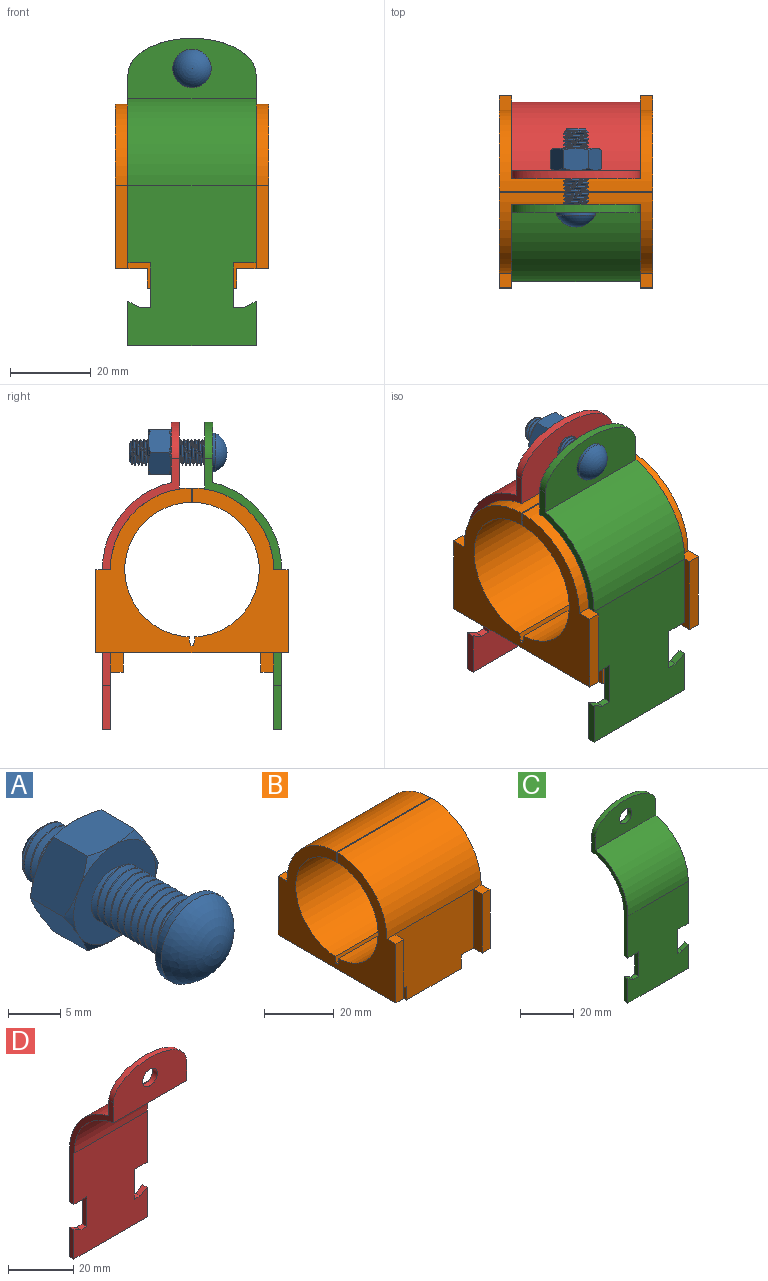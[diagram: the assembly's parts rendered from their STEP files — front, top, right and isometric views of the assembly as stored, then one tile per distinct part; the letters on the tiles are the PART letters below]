
ASSEMBLY  parts=4 mates=3
PART A: 34 faces, bbox 13.4x25x13.4 mm
  f0: cylinder r=3.17mm len=10.32mm, axis (0,-1,0), area 25.9mm2, adj f1,f3,f4,f8
  f1: bspline ~11.11x6.35mm, area 140.6mm2, adj f0,f2,f4,f8
  f2: cylinder r=2.59mm len=10.32mm, axis (0,-1,0), area 21.1mm2, adj f1,f3,f4,f8
  f3: bspline ~11.11x6.35mm, area 140.6mm2, adj f0,f2,f4,f8
  f4: plane 9.89x9.89mm, normal (0,1,0), area 45.1mm2, adj f0,f1,f2,f3,f5
  f5: cylinder r=4.76mm len=9.53mm, axis (0,1,0), area 22.8mm2, adj f4,f6
  f6: sphere r=5.32mm, area 98.5mm2, adj f5
  f7: plane 11.47x11.47mm, normal (0,1,0), area 70.8mm2, adj f15,f16,f17,f18,f19,f20,f30,f31
  f8: plane 11.47x11.47mm, normal (0,-1,0), area 70.8mm2, adj f0,f1,f2,f3,f21,f22,f23,f24
  f9: plane 6.09x6.08mm, normal (-0.87,0,0.5), area 33.4mm2, adj f10,f14,f15,f16,f21,f22
  f10: plane 6.95x6.08mm, normal (0,0,1), area 33.4mm2, adj f9,f11,f15,f20,f21,f26
  f11: plane 6.09x6.08mm, normal (0.87,0,0.5), area 33.4mm2, adj f10,f12,f19,f20,f25,f26
  f12: plane 6.09x6.08mm, normal (0.87,0,-0.5), area 33.4mm2, adj f11,f13,f18,f19,f24,f25
  f13: plane 6.95x6.08mm, normal (0,0,-1), area 33.4mm2, adj f12,f14,f17,f18,f23,f24
  f14: plane 6.09x6.08mm, normal (-0.87,0,-0.5), area 33.4mm2, adj f9,f13,f16,f17,f22,f23
  f15: cone r=5.56mm half-angle=60deg, axis (0,-1,0), area 3mm2, adj f7,f9,f10
  f16: cone r=5.56mm half-angle=60deg, axis (0,-1,0), area 3mm2, adj f7,f9,f14
  f17: cone r=5.56mm half-angle=60deg, axis (0,-1,0), area 3mm2, adj f7,f13,f14
  f18: cone r=5.56mm half-angle=60deg, axis (0,-1,0), area 3mm2, adj f7,f12,f13
  f19: cone r=5.56mm half-angle=60deg, axis (0,-1,0), area 3mm2, adj f7,f11,f12
  f20: cone r=5.56mm half-angle=60deg, axis (0,-1,0), area 3mm2, adj f7,f10,f11
  f21: cone r=5.56mm half-angle=60deg, axis (0,1,0), area 3mm2, adj f8,f9,f10
  f22: cone r=5.56mm half-angle=60deg, axis (0,1,0), area 3mm2, adj f8,f9,f14
  f23: cone r=5.56mm half-angle=60deg, axis (0,1,0), area 3mm2, adj f8,f13,f14
  f24: cone r=5.56mm half-angle=60deg, axis (0,1,0), area 3mm2, adj f8,f12,f13
  f25: cone r=5.56mm half-angle=60deg, axis (0,1,0), area 3mm2, adj f8,f11,f12
  f26: cone r=5.56mm half-angle=60deg, axis (0,1,0), area 3mm2, adj f8,f10,f11
  f27: plane 4.54x4.54mm, normal (0,1,0), area 16.2mm2, adj f28
  f28: cone r=3.17mm half-angle=45deg, axis (0,-1,0), area 12.5mm2, adj f27,f29,f30,f31,f32
  f29: cone r=3.17mm half-angle=45deg, axis (0,-1,0), area 1.7mm2, adj f28,f30,f32,f33
  f30: bspline ~6.35x6.35mm, area 56.5mm2, adj f7,f28,f29,f31,f33
  f31: cylinder r=2.59mm len=5.17mm, axis (0,-1,0), area 9.1mm2, adj f7,f28,f30,f32
  f32: bspline ~6.35x6.35mm, area 56.2mm2, adj f7,f28,f29,f31,f33
  f33: cylinder r=3.17mm len=6.35mm, axis (0,-1,0), area 9.6mm2, adj f7,f29,f30,f32
PART B: 35 faces, bbox 38.1x47.6x45.6 mm
  f0: plane 20.64x3.18mm, normal (0,-1,0), area 65.5mm2, adj f1,f11,f25,f30
  f1: plane 3.57x3.18mm, normal (0,0,1), area 11.3mm2, adj f0,f23,f25,f30
  f2: plane 20.64x3.18mm, normal (0,1,0), area 65.5mm2, adj f3,f11,f25,f28
  f3: plane 3.57x3.18mm, normal (0,0,1), area 11.3mm2, adj f2,f14,f25,f28
  f4: plane 20.64x3.18mm, normal (0,-1,0), area 65.5mm2, adj f11,f24,f26,f29
  f5: plane 31.75x25.4mm, normal (0,-1,0), area 760.8mm2, adj f6,f11,f23,f29,f30,f31,f33
  f6: plane 22.17x3.18mm, normal (0,0,-1), area 70.4mm2, adj f5,f7,f31,f33
  f7: plane 22.17x4.76mm, normal (0,1,0), area 105.6mm2, adj f6,f11,f31,f33
  f8: plane 22.17x4.76mm, normal (0,-1,0), area 105.6mm2, adj f9,f11,f32,f34
  f9: plane 22.17x3.18mm, normal (0,0,-1), area 70.4mm2, adj f8,f10,f32,f34
  f10: plane 31.75x25.4mm, normal (0,1,0), area 760.8mm2, adj f9,f11,f14,f27,f28,f32,f34
  f11: plane 47.63x38.1mm, normal (0,0,-1), area 1446.9mm2, adj f0,f2,f4,f5,f7,f8,f10,f12
  f12: plane 20.64x3.18mm, normal (0,1,0), area 65.5mm2, adj f11,f13,f26,f27
  f13: plane 3.57x3.18mm, normal (0,0,1), area 11.3mm2, adj f12,f14,f26,f27
  f14: cylinder r=20.24mm len=38.1mm, axis (-1,0,0), area 1206.5mm2, adj f3,f10,f13,f15,f25,f26
  f15: plane 38.1x3.57mm, normal (0,-1,0), area 136.1mm2, adj f14,f16,f25,f26
  f16: cylinder r=16.67mm len=38.1mm, axis (-1,0,0), area 1962.7mm2, adj f15,f17,f25,f26
  f17: plane 38.1x2.12mm, normal (0,-0.99,0.15), area 81.9mm2, adj f16,f18,f25,f26
  f18: plane 38.1x0.39mm, normal (0,-0.25,0.97), area 15.5mm2, adj f17,f19,f25,f26
  f19: plane 38.1x0.39mm, normal (0,0.25,0.97), area 15.5mm2, adj f18,f20,f25,f26
  f20: plane 38.1x2.12mm, normal (0,0.99,0.15), area 81.9mm2, adj f19,f21,f25,f26
  f21: cylinder r=16.67mm len=38.1mm, axis (-1,0,0), area 1962.7mm2, adj f20,f22,f25,f26
  f22: plane 38.1x3.57mm, normal (0,1,0), area 136.1mm2, adj f21,f23,f25,f26
  f23: cylinder r=20.24mm len=38.1mm, axis (-1,0,0), area 1206.5mm2, adj f1,f5,f22,f24,f25,f26
  f24: plane 3.57x3.18mm, normal (0,0,1), area 11.3mm2, adj f4,f23,f26,f29
  f25: plane 47.63x40.88mm, normal (1,0,0), area 750.2mm2, adj f0,f1,f2,f3,f11,f14,f15,f16
  f26: plane 47.63x40.88mm, normal (-1,0,0), area 750.2mm2, adj f4,f11,f12,f13,f14,f15,f16,f17
  f27: plane 20.64x3.57mm, normal (1,0,0), area 73.7mm2, adj f10,f11,f12,f13
  f28: plane 20.64x3.57mm, normal (-1,0,0), area 73.7mm2, adj f2,f3,f10,f11
  f29: plane 20.64x3.57mm, normal (1,0,0), area 73.7mm2, adj f4,f5,f11,f24
  f30: plane 20.64x3.57mm, normal (-1,0,0), area 73.7mm2, adj f0,f1,f5,f11
  f31: plane 4.76x3.18mm, normal (-1,0,0), area 15.1mm2, adj f5,f6,f7,f11
  f32: plane 4.76x3.18mm, normal (-1,0,0), area 15.1mm2, adj f8,f9,f10,f11
  f33: plane 4.76x3.18mm, normal (1,0,0), area 15.1mm2, adj f5,f6,f7,f11
  f34: plane 4.76x3.18mm, normal (1,0,0), area 15.1mm2, adj f8,f9,f10,f11
PART C: 21 faces, bbox 31.8x19.1x76.2 mm
  f0: plane 46.65x19.05mm, normal (-1,0,0), area 109.1mm2, adj f1,f13,f14,f15,f16,f17,f18,f20
  f1: plane 5.55x1.98mm, normal (0,0,-1), area 11mm2, adj f0,f2,f13,f16
  f2: plane 11.13x1.98mm, normal (-1,0,0), area 22.1mm2, adj f1,f3,f13,f16
  f3: plane 2.54x1.98mm, normal (0,0,1), area 5mm2, adj f2,f4,f13,f16
  f4: plane 3.01x1.98mm, normal (0.47,0,0.89), area 6.7mm2, adj f3,f5,f13,f16
  f5: plane 10.97x1.98mm, normal (-1,0,0), area 21.8mm2, adj f4,f6,f13,f16
  f6: plane 31.75x1.98mm, normal (0,0,-1), area 63mm2, adj f5,f7,f13,f16
  f7: plane 10.97x1.98mm, normal (1,0,0), area 21.8mm2, adj f6,f8,f13,f16
  f8: plane 3.01x1.98mm, normal (-0.47,0,0.89), area 6.7mm2, adj f7,f9,f13,f16
  f9: plane 2.54x1.98mm, normal (0,0,1), area 5mm2, adj f8,f10,f13,f16
  f10: plane 11.13x1.98mm, normal (1,0,0), area 22.1mm2, adj f9,f11,f13,f16
  f11: plane 5.55x1.98mm, normal (0,0,-1), area 11mm2, adj f10,f12,f13,f16
  f12: plane 46.65x19.05mm, normal (1,0,0), area 109.1mm2, adj f11,f13,f14,f15,f16,f17,f18,f20
  f13: plane 39.68x31.75mm, normal (0,-1,0), area 1140.9mm2, adj f0,f1,f2,f3,f4,f5,f6,f7
  f14: plane 31.75x14.91mm, normal (0,-1,0), area 380.1mm2, adj f0,f12,f15,f19,f20
  f15: cylinder r=22.23mm len=31.75mm, axis (1,0,0), area 943.1mm2, adj f0,f12,f13,f14
  f16: plane 39.68x31.75mm, normal (0,1,0), area 1140.9mm2, adj f0,f1,f2,f3,f4,f5,f6,f7
  f17: cylinder r=20.24mm len=31.75mm, axis (1,0,0), area 908.2mm2, adj f0,f12,f16,f18
  f18: plane 31.75x16.54mm, normal (0,1,0), area 431.8mm2, adj f0,f12,f17,f19,f20
  f19: cylinder r=3.17mm len=6.35mm, axis (0,-1,0), area 39.6mm2, adj f14,f18
  f20: extruded ~31.75x9.04mm, area 79.1mm2, adj f0,f12,f14,f18
PART D: 21 faces, bbox 31.8x19.1x76.2 mm
  f0: plane 46.65x19.05mm, normal (-1,0,0), area 109.1mm2, adj f1,f13,f14,f15,f16,f17,f18,f20
  f1: plane 39.68x31.75mm, normal (0,1,0), area 1140.9mm2, adj f0,f2,f3,f4,f5,f6,f7,f8
  f2: plane 46.65x19.05mm, normal (1,0,0), area 109.1mm2, adj f1,f3,f14,f15,f16,f17,f18,f20
  f3: plane 5.55x1.98mm, normal (0,0,-1), area 11mm2, adj f1,f2,f4,f14
  f4: plane 11.13x1.98mm, normal (1,0,0), area 22.1mm2, adj f1,f3,f5,f14
  f5: plane 2.54x1.98mm, normal (0,0,1), area 5mm2, adj f1,f4,f6,f14
  f6: plane 3.01x1.98mm, normal (-0.47,0,0.89), area 6.7mm2, adj f1,f5,f7,f14
  f7: plane 10.97x1.98mm, normal (1,0,0), area 21.8mm2, adj f1,f6,f8,f14
  f8: plane 31.75x1.98mm, normal (0,0,-1), area 63mm2, adj f1,f7,f9,f14
  f9: plane 10.97x1.98mm, normal (-1,0,0), area 21.8mm2, adj f1,f8,f10,f14
  f10: plane 3.01x1.98mm, normal (0.47,0,0.89), area 6.7mm2, adj f1,f9,f11,f14
  f11: plane 2.54x1.98mm, normal (0,0,1), area 5mm2, adj f1,f10,f12,f14
  f12: plane 11.13x1.98mm, normal (-1,0,0), area 22.1mm2, adj f1,f11,f13,f14
  f13: plane 5.55x1.98mm, normal (0,0,-1), area 11mm2, adj f0,f1,f12,f14
  f14: plane 39.68x31.75mm, normal (0,-1,0), area 1140.9mm2, adj f0,f2,f3,f4,f5,f6,f7,f8
  f15: cylinder r=20.24mm len=31.75mm, axis (1,0,0), area 908.2mm2, adj f0,f2,f14,f16
  f16: plane 31.75x16.54mm, normal (0,-1,0), area 431.8mm2, adj f0,f2,f15,f19,f20
  f17: cylinder r=22.23mm len=31.75mm, axis (1,0,0), area 943.1mm2, adj f0,f1,f2,f18
  f18: plane 31.75x14.91mm, normal (0,1,0), area 380.1mm2, adj f0,f2,f17,f19,f20
  f19: cylinder r=3.17mm len=6.35mm, axis (0,-1,0), area 39.6mm2, adj f16,f18
  f20: extruded ~31.75x9.04mm, area 79.1mm2, adj f0,f2,f16,f18
PLACE A t=(-14.78,-135.64,-63.45)mm
PLACE B t=(-14.78,-135.74,-63.45)mm
PLACE C t=(-14.78,-135.74,-63.45)mm
PLACE D t=(-14.78,-135.74,-63.45)mm
MATE fastened A.f0 <-> D.f19  axis (0,1,0) through (-14.78,-120.16,-34.38)mm
MATE fastened B.f14 <-> C.f15  axis (-1,0,0) through (-14.78,-135.74,-63.45)mm
MATE fastened D.f15 <-> B.f14  axis (1,0,0) through (1.09,-135.74,-63.45)mm
